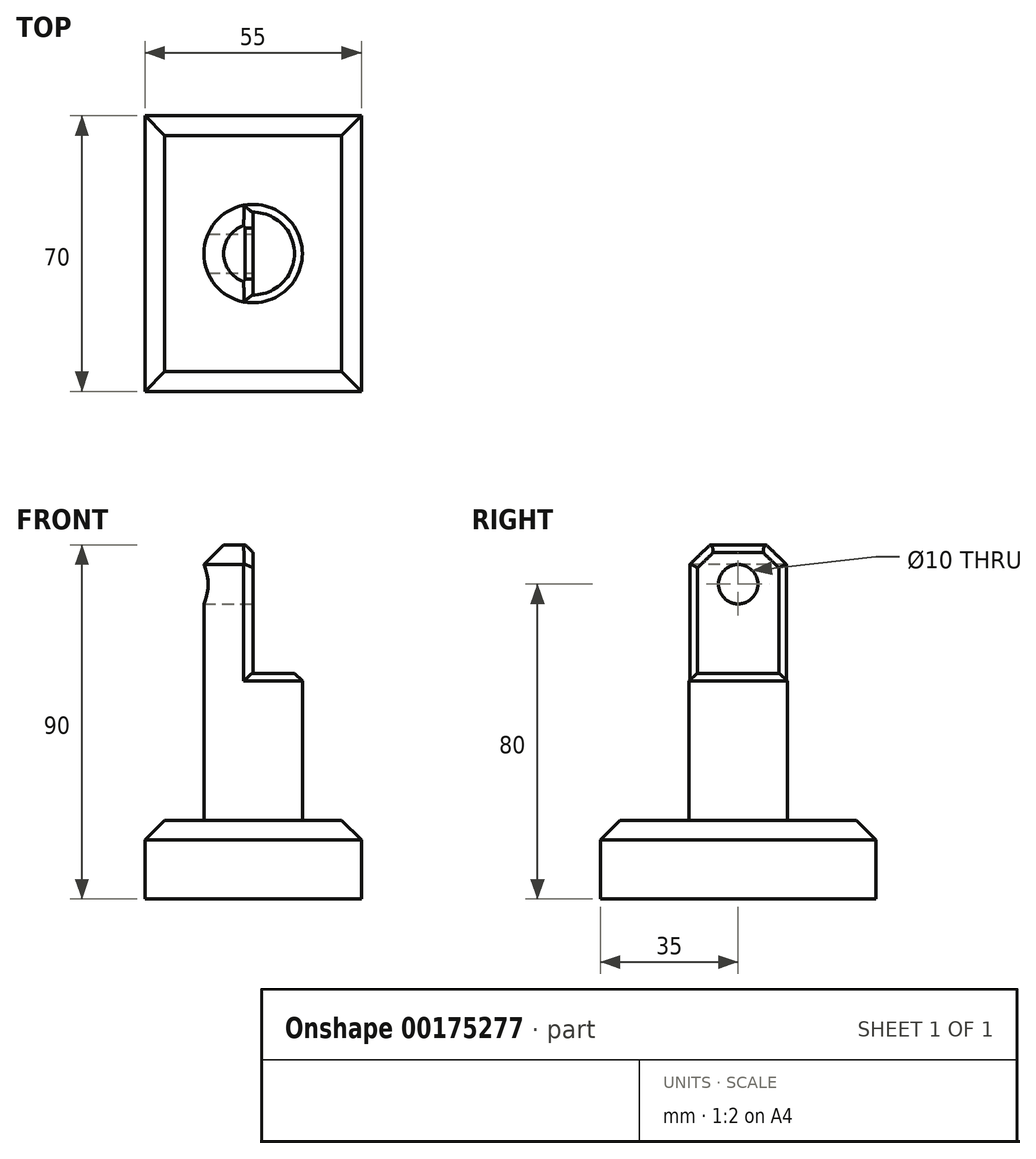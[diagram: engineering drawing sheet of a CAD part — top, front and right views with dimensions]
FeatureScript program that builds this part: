
annotation { "Feature Type Name" : "Feature", "Feature Type Description" : "" }
export const myFeature = defineFeature(function(context is Context, id is Id, definition is map)
    precondition{}
    {
        {
            var Q0;
            Q0=qCreatedBy(makeId("Top.planeOp"),FACE);
            var sketch = newSketch(context, id + "F0", { "sketchPlane" : qUnion([Q0])});
            skLineSegment(sketch, "E0.bottom", {"start": v(-27.5, 35) * mm, "end": v(27.5, 35) * mm});
            skLineSegment(sketch, "E0.top", {"start": v(-27.5, -35) * mm, "end": v(27.5, -35) * mm});
            skLineSegment(sketch, "E0.left", {"start": v(-27.5, 35) * mm, "end": v(-27.5, -35) * mm});
            skLineSegment(sketch, "E0.right", {"start": v(27.5, 35) * mm, "end": v(27.5, -35) * mm});
            skLineSegment(sketch, "E1", {"start": v(-27.5, 35) * mm, "end": v(27.5, -35) * mm, "construction": true});
            skSolve(sketch);
        }
        {
            var Q0;
            Q0 = qSketchRegion(id + "F0", true);
            extrude(context, id + "F1", {"entities" : qUnion([Q0]), "depth" : 20 * mm});
        }
        {
            var Q0;
            Q0=makeQuery(id+"F1.opExtrude","CAP_FACE",FACE,{"disambiguationData":[OSD([sQuery(id+"F0.wireOp",EDGE,"E0.bottom"),sQuery(id+"F0.wireOp",EDGE,"E0.top"),sQuery(id+"F0.wireOp",EDGE,"E0.left"),sQuery(id+"F0.wireOp",EDGE,"E0.right")])],"isStart":false});
            var sketch = newSketch(context, id + "F2", { "sketchPlane" : qUnion([Q0])});
            skCircle(sketch, "E2", {"center": v(0, 0) * mm, "radius": 12.5 * mm});
            skSolve(sketch);
        }
        {
            var Q0;
            Q0 = qSketchRegion(id + "F2", true);
            extrude(context, id + "F3", {"entities" : qUnion([Q0]), "operationType" : NewBodyOperationType.ADD, "depth" : 70 * mm});
        }
        {
            var Q0;
            Q0=makeQuery(id+"F3.opExtrude","CAP_EDGE",EDGE,{"disambiguationData":[OSD([sQuery(id+"F2.wireOp",EDGE,"E2")])],"isStart":false});
            chamfer(context, id + "F4", {"entities" : qUnion([Q0]), "width" : 5 * mm, "tangentPropagation" : true});
        }
        {
            var Q0;
            Q0=makeQuery(id+"F1.opExtrude","CAP_EDGE",EDGE,{"disambiguationData":[OSD([sQuery(id+"F0.wireOp",EDGE,"E0.top")])],"isStart":false});
            var Q1;
            Q1=makeQuery(id+"F1.opExtrude","CAP_EDGE",EDGE,{"disambiguationData":[OSD([sQuery(id+"F0.wireOp",EDGE,"E0.left")])],"isStart":false});
            var Q2;
            Q2=makeQuery(id+"F1.opExtrude","CAP_EDGE",EDGE,{"disambiguationData":[OSD([sQuery(id+"F0.wireOp",EDGE,"E0.bottom")])],"isStart":false});
            var Q3;
            Q3=makeQuery(id+"F1.opExtrude","CAP_EDGE",EDGE,{"disambiguationData":[OSD([sQuery(id+"F0.wireOp",EDGE,"E0.right")])],"isStart":false});
            chamfer(context, id + "F5", {"entities" : qUnion([Q0, Q1, Q2, Q3]), "width" : 5 * mm, "tangentPropagation" : true});
        }
        {
            var Q0;
            Q0=qCreatedBy(makeId("Right.planeOp"),FACE);
            var sketch = newSketch(context, id + "F6", { "sketchPlane" : qUnion([Q0])});
            skLineSegment(sketch, "E3.bottom", {"start": v(24.53, 57.39) * mm, "end": v(-25.48, 57.39) * mm});
            skLineSegment(sketch, "E3.top", {"start": v(24.53, 98.13) * mm, "end": v(-25.48, 98.13) * mm});
            skLineSegment(sketch, "E3.left", {"start": v(24.53, 57.39) * mm, "end": v(24.53, 98.13) * mm});
            skLineSegment(sketch, "E3.right", {"start": v(-25.48, 57.39) * mm, "end": v(-25.48, 98.13) * mm});
            skPoint(sketch, "E3.middle", {"position": v(-0.47, 77.76) * mm});
            skSolve(sketch);
        }
        {
            var Q0;
            Q0 = qSketchRegion(id + "F6", true);
            extrude(context, id + "F7", {"entities" : qUnion([Q0]), "operationType" : NewBodyOperationType.REMOVE, "depth" : 25 * mm});
        }
        {
            var Q0;
            Q0=makeQuery(id+"F7.boolean.opBoolean","COPY",FACE,{"derivedFrom":makeQuery(id+"F7.opExtrude","CAP_FACE",FACE,{"disambiguationData":[OSD([sQuery(id+"F6.wireOp",EDGE,"E3.bottom"),sQuery(id+"F6.wireOp",EDGE,"E3.top"),sQuery(id+"F6.wireOp",EDGE,"E3.left"),sQuery(id+"F6.wireOp",EDGE,"E3.right")])],"isStart":true})});
            var sketch = newSketch(context, id + "F8", { "sketchPlane" : qUnion([Q0])});
            skCircle(sketch, "E4", {"center": v(0, 80) * mm, "radius": 5 * mm});
            skLineSegment(sketch, "E5", {"start": v(0, 90) * mm, "end": v(0, 64.08) * mm, "construction": true});
            skSolve(sketch);
        }
        {
            var Q0;
            Q0 = qSketchRegion(id + "F8", true);
            extrude(context, id + "F9", {"entities" : qUnion([Q0]), "operationType" : NewBodyOperationType.REMOVE, "oppositeDirection" : true, "depth" : 25 * mm});
        }
        {
            var Q0;
            Q0=makeQuery(id+"F7.boolean.opBoolean","INTERSECT",EDGE,{"disambiguationData":[OD(1.0)],"derivedFrom":[makeQuery(id+"F3.opExtrude","SWEPT_FACE",FACE,{"disambiguationData":[OSD([sQuery(id+"F2.wireOp",EDGE,"E2")])]}),makeQuery(id+"F7.opExtrude","CAP_FACE",FACE,{"disambiguationData":[OSD([sQuery(id+"F6.wireOp",EDGE,"E3.bottom"),sQuery(id+"F6.wireOp",EDGE,"E3.top"),sQuery(id+"F6.wireOp",EDGE,"E3.left"),sQuery(id+"F6.wireOp",EDGE,"E3.right")])],"isStart":true})]});
            var Q1;
            Q1=makeQuery(id+"F7.boolean.opBoolean","INTERSECT",EDGE,{"disambiguationData":[OD(1.0)],"derivedFrom":[makeQuery(id+"F4.opChamfer","BLEND_FACE",FACE,{"disambiguationData":[OSD([sQuery(id+"F2.wireOp",EDGE,"E2")])]}),makeQuery(id+"F7.opExtrude","CAP_FACE",FACE,{"disambiguationData":[OSD([sQuery(id+"F6.wireOp",EDGE,"E3.bottom"),sQuery(id+"F6.wireOp",EDGE,"E3.top"),sQuery(id+"F6.wireOp",EDGE,"E3.left"),sQuery(id+"F6.wireOp",EDGE,"E3.right")])],"isStart":true})]});
            var Q2;
            Q2=makeQuery(id+"F7.boolean.opBoolean","INTERSECT",EDGE,{"derivedFrom":[makeQuery(id+"F3.opExtrude","CAP_FACE",FACE,{"disambiguationData":[OSD([sQuery(id+"F2.wireOp",EDGE,"E2")])],"isStart":false}),makeQuery(id+"F7.opExtrude","CAP_FACE",FACE,{"disambiguationData":[OSD([sQuery(id+"F6.wireOp",EDGE,"E3.bottom"),sQuery(id+"F6.wireOp",EDGE,"E3.top"),sQuery(id+"F6.wireOp",EDGE,"E3.left"),sQuery(id+"F6.wireOp",EDGE,"E3.right")])],"isStart":true})]});
            var Q3;
            Q3=makeQuery(id+"F7.boolean.opBoolean","INTERSECT",EDGE,{"disambiguationData":[OD(0.0)],"derivedFrom":[makeQuery(id+"F4.opChamfer","BLEND_FACE",FACE,{"disambiguationData":[OSD([sQuery(id+"F2.wireOp",EDGE,"E2")])]}),makeQuery(id+"F7.opExtrude","CAP_FACE",FACE,{"disambiguationData":[OSD([sQuery(id+"F6.wireOp",EDGE,"E3.bottom"),sQuery(id+"F6.wireOp",EDGE,"E3.top"),sQuery(id+"F6.wireOp",EDGE,"E3.left"),sQuery(id+"F6.wireOp",EDGE,"E3.right")])],"isStart":true})]});
            var Q4;
            Q4=makeQuery(id+"F7.boolean.opBoolean","INTERSECT",EDGE,{"disambiguationData":[OD(0.0)],"derivedFrom":[makeQuery(id+"F3.opExtrude","SWEPT_FACE",FACE,{"disambiguationData":[OSD([sQuery(id+"F2.wireOp",EDGE,"E2")])]}),makeQuery(id+"F7.opExtrude","CAP_FACE",FACE,{"disambiguationData":[OSD([sQuery(id+"F6.wireOp",EDGE,"E3.bottom"),sQuery(id+"F6.wireOp",EDGE,"E3.top"),sQuery(id+"F6.wireOp",EDGE,"E3.left"),sQuery(id+"F6.wireOp",EDGE,"E3.right")])],"isStart":true})]});
            var Q5;
            Q5=makeQuery(id+"F7.boolean.opBoolean","INTERSECT",EDGE,{"derivedFrom":[makeQuery(id+"F3.opExtrude","SWEPT_FACE",FACE,{"disambiguationData":[OSD([sQuery(id+"F2.wireOp",EDGE,"E2")])]}),makeQuery(id+"F7.opExtrude","SWEPT_FACE",FACE,{"disambiguationData":[OSD([sQuery(id+"F6.wireOp",EDGE,"E3.bottom")])]})]});
            chamfer(context, id + "F10", {"entities" : qUnion([Q0, Q1, Q2, Q3, Q4, Q5]), "width" : 2 * mm, "tangentPropagation" : true});
        }
    });
